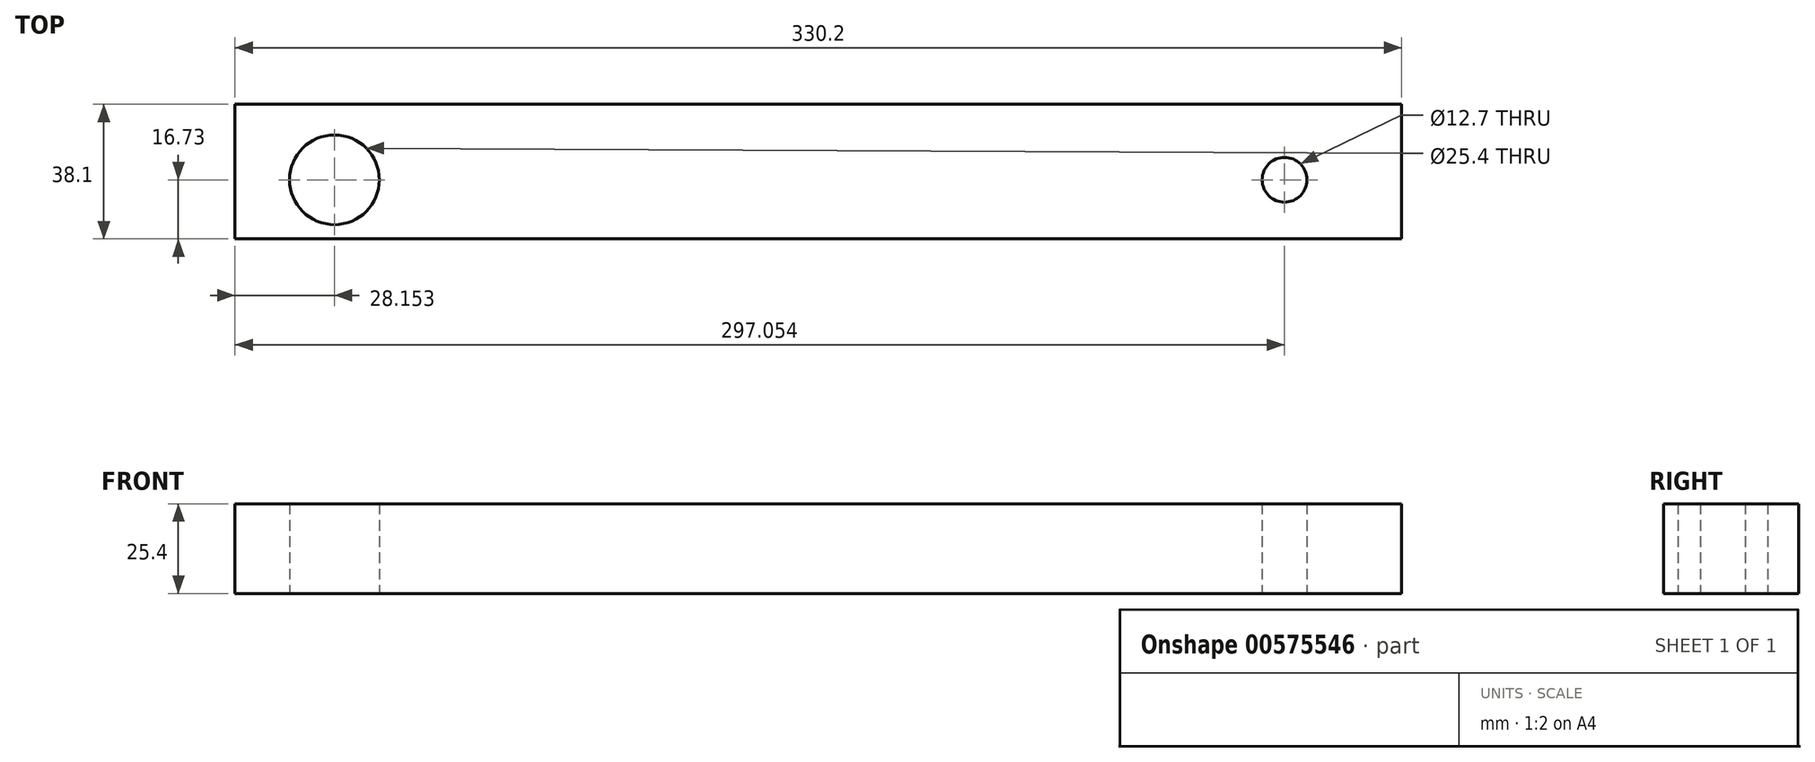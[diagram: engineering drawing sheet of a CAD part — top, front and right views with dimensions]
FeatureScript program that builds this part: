
annotation { "Feature Type Name" : "Feature", "Feature Type Description" : "" }
export const myFeature = defineFeature(function(context is Context, id is Id, definition is map)
    precondition{}
    {
        {
            var Q0;
            Q0=qCreatedBy(makeId("Top.planeOp"),FACE);
            var sketch = newSketch(context, id + "F0", { "sketchPlane" : qUnion([Q0])});
            skLineSegment(sketch, "E0.bottom", {"start": v(-163.22, 21.37) * mm, "end": v(166.98, 21.37) * mm});
            skLineSegment(sketch, "E0.top", {"start": v(-163.22, -16.73) * mm, "end": v(166.98, -16.73) * mm});
            skLineSegment(sketch, "E0.left", {"start": v(-163.22, 21.37) * mm, "end": v(-163.22, -16.73) * mm});
            skLineSegment(sketch, "E0.right", {"start": v(166.98, 21.37) * mm, "end": v(166.98, -16.73) * mm});
            skSolve(sketch);
        }
        {
            var Q0;
            Q0=qCreatedBy(makeId("Top.planeOp"),FACE);
            var sketch = newSketch(context, id + "F1", { "sketchPlane" : qUnion([Q0])});
            skCircle(sketch, "E1", {"center": v(-135.07, 0) * mm, "radius": 12.7 * mm});
            skCircle(sketch, "E2", {"center": v(133.83, 0) * mm, "radius": 6.35 * mm});
            skSolve(sketch);
        }
        {
            var Q0;
            Q0 = qSketchRegion(id + "F0", true);
            extrude(context, id + "F2", {"entities" : qUnion([Q0]), "endBound" : BoundingType.SYMMETRIC, "depth" : 25.4 * mm, "offsetDistance" : 25.4 * mm});
        }
        {
            var Q0;
            Q0 = qSketchRegion(id + "F1", true);
            extrude(context, id + "F3", {"entities" : qUnion([Q0]), "operationType" : NewBodyOperationType.REMOVE, "endBound" : BoundingType.SYMMETRIC, "depth" : 25.4 * mm, "offsetDistance" : 25.4 * mm});
        }
    });
